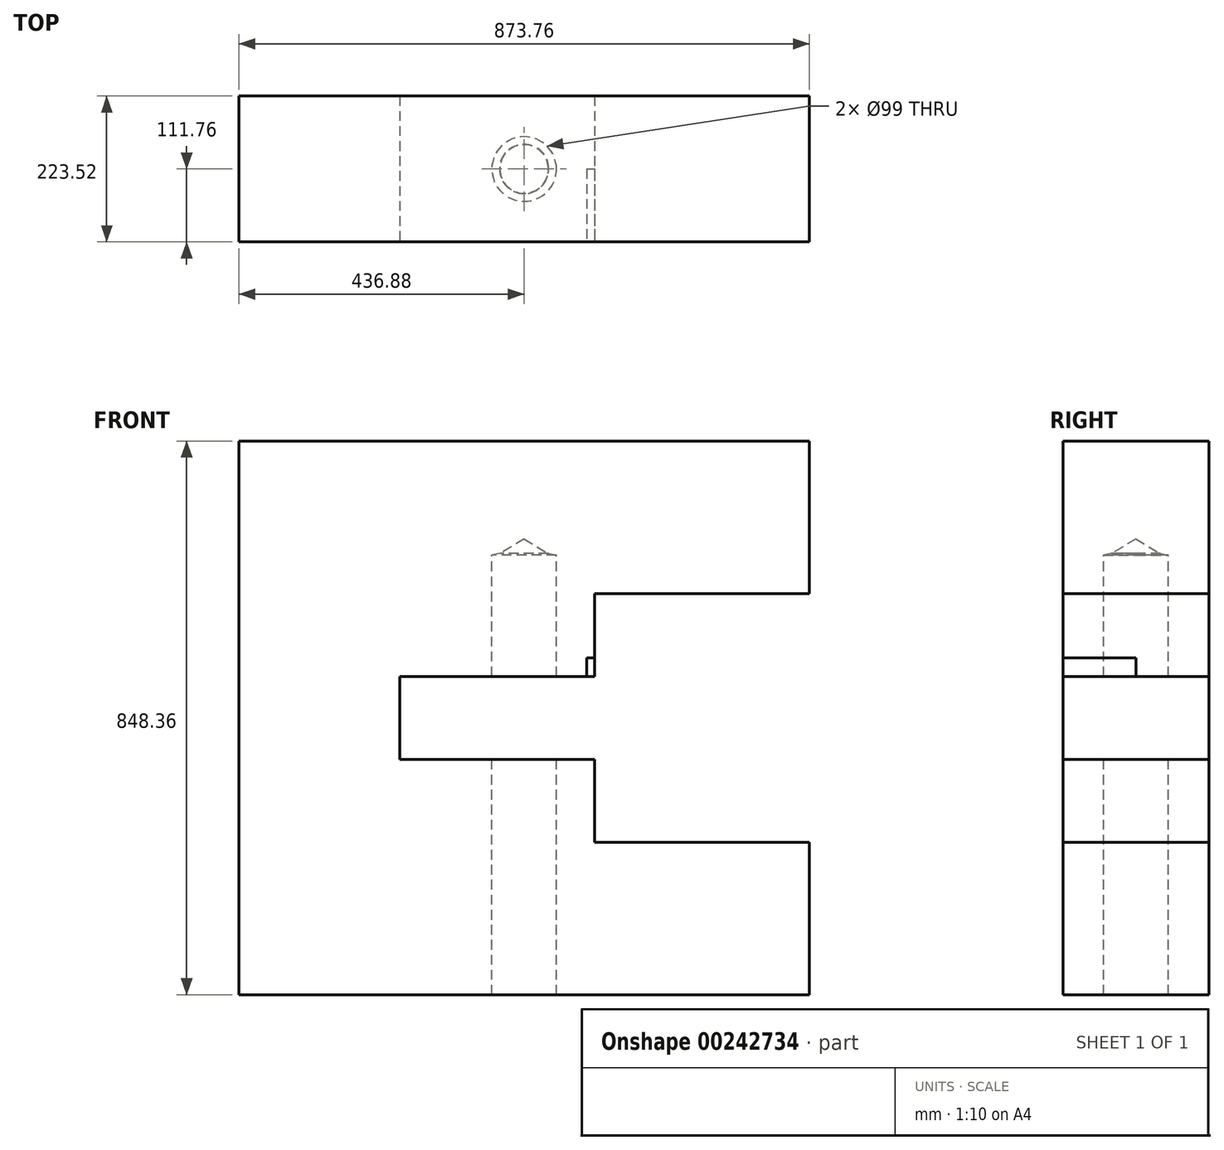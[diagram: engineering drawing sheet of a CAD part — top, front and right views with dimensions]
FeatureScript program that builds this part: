
annotation { "Feature Type Name" : "Feature", "Feature Type Description" : "" }
export const myFeature = defineFeature(function(context is Context, id is Id, definition is map)
    precondition{}
    {
        {
            var Q0;
            Q0=qCreatedBy(makeId("Front.planeOp"),FACE);
            var sketch = newSketch(context, id + "F0", { "sketchPlane" : qUnion([Q0])});
            skLineSegment(sketch, "E0.bottom", {"start": v(-436.88, -424.18) * mm, "end": v(436.88, -424.18) * mm});
            skLineSegment(sketch, "E0.top", {"start": v(-436.88, 424.18) * mm, "end": v(436.88, 424.18) * mm});
            skLineSegment(sketch, "E0.left", {"start": v(-436.88, -424.18) * mm, "end": v(-436.88, 424.18) * mm});
            skLineSegment(sketch, "E0.right", {"start": v(436.88, -424.18) * mm, "end": v(436.88, 424.18) * mm});
            skPoint(sketch, "E0.middle", {"position": v(0, 0) * mm});
            skSolve(sketch);
        }
        {
            var Q0;
            Q0 = qSketchRegion(id + "F0", true);
            extrude(context, id + "F1", {"entities" : qUnion([Q0]), "depth" : 223.52 * mm});
        }
        {
            var Q0;
            Q0=makeQuery(id+"F1.opExtrude","CAP_FACE",FACE,{"disambiguationData":[OSD([sQuery(id+"F0.wireOp",EDGE,"E0.bottom"),sQuery(id+"F0.wireOp",EDGE,"E0.top"),sQuery(id+"F0.wireOp",EDGE,"E0.left"),sQuery(id+"F0.wireOp",EDGE,"E0.right")])],"isStart":false});
            var sketch = newSketch(context, id + "F2", { "sketchPlane" : qUnion([Q0])});
            skLineSegment(sketch, "E1.0", {"start": v(107.7, 63.5) * mm, "end": v(-190.5, 63.5) * mm});
            skLineSegment(sketch, "E2", {"start": v(-190.5, 48.9) * mm, "end": v(-190.5, 0) * mm});
            skLineSegment(sketch, "E3", {"start": v(-190.5, 48.9) * mm, "end": v(-190.5, 63.5) * mm});
            skLineSegment(sketch, "E4", {"start": v(107.7, 181.23) * mm, "end": v(107.7, 85.35) * mm});
            skLineSegment(sketch, "E5", {"start": v(107.7, 190.5) * mm, "end": v(430.53, 190.5) * mm});
            skLineSegment(sketch, "E6", {"start": v(107.7, 85.35) * mm, "end": v(107.7, 63.5) * mm});
            skLineSegment(sketch, "E7", {"start": v(107.7, 181.23) * mm, "end": v(107.7, 190.5) * mm});
            skPoint(sketch, "E8.orphan", {"position": v(0, 63.5) * mm});
            skPoint(sketch, "E9.orphan", {"position": v(107.7, 0) * mm});
            skLineSegment(sketch, "E10.MirrorCS", {"start": v(107.7, -190.5) * mm, "end": v(716.46, -190.5) * mm});
            skLineSegment(sketch, "E11.MirrorCS", {"start": v(107.7, -181.23) * mm, "end": v(107.7, -85.35) * mm});
            skLineSegment(sketch, "E12.MirrorCS", {"start": v(107.7, -63.5) * mm, "end": v(-190.5, -63.5) * mm});
            skLineSegment(sketch, "E13.MirrorCS", {"start": v(107.7, -85.35) * mm, "end": v(107.7, -63.5) * mm});
            skLineSegment(sketch, "E14.MirrorCS", {"start": v(-190.5, -48.9) * mm, "end": v(-190.5, -63.5) * mm});
            skLineSegment(sketch, "E15.MirrorCS", {"start": v(-190.5, -48.9) * mm, "end": v(-190.5, 0) * mm});
            skLineSegment(sketch, "E16", {"start": v(430.53, 190.5) * mm, "end": v(716.46, 190.5) * mm});
            skLineSegment(sketch, "E17", {"start": v(716.46, 190.5) * mm, "end": v(716.46, -190.5) * mm});
            skLineSegment(sketch, "E18", {"start": v(107.7, -181.23) * mm, "end": v(107.7, -190.5) * mm});
            skSolve(sketch);
        }
        {
            var Q0;
            Q0 = qSketchRegion(id + "F2", true);
            extrude(context, id + "F3", {"entities" : qUnion([Q0]), "operationType" : NewBodyOperationType.REMOVE, "oppositeDirection" : true, "depth" : 254 * mm});
        }
        {
            var Q0;
            Q0=makeQuery(id+"F1.opExtrude","SWEPT_FACE",FACE,{"disambiguationData":[OSD([sQuery(id+"F0.wireOp",EDGE,"E0.bottom")])]});
            var sketch = newSketch(context, id + "F4", { "sketchPlane" : qUnion([Q0])});
            skPoint(sketch, "E19", {"position": v(0, 111.76) * mm});
            skLineSegment(sketch, "E20", {"start": v(-436.88, 111.76) * mm, "end": v(436.88, 111.76) * mm});
            skCircle(sketch, "E21", {"center": v(0, 111.76) * mm, "radius": 49.53 * mm});
            skSolve(sketch);
        }
        {
            var Q0;
            Q0=sQuery(id+"F4.wireOp",VERTEX,"E19");
            var Q1;
            Q1=makeQuery(id+"F1.opExtrude","SWEPT_BODY",BODY,{"disambiguationData":[OSD([sQuery(id+"F0.wireOp",EDGE,"E0.bottom"),sQuery(id+"F0.wireOp",EDGE,"E0.top"),sQuery(id+"F0.wireOp",EDGE,"E0.left"),sQuery(id+"F0.wireOp",EDGE,"E0.right")])]});
            hole(context, id + "F5", {"style" : HoleStyle.SIMPLE, "endStyle" : HoleEndStyle.BLIND, "holeDiameter" : 75 * mm, "holeDepth" : 675.64 * mm, "locations" : qUnion([Q0]), "scope" : qUnion([Q1]), "tappedDepth" : 12 * mm, "tapClearance" : 3});
        }
        {
            var Q0;
            Q0=qCreatedBy(makeId("Front.planeOp"),FACE);
            cPlane(context, id + "F6", {"entities" : qUnion([Q0]), "cplaneType" : CPlaneType.OFFSET, "offset" : 111.76 * mm, "width" : 152.4 * mm, "height" : 152.4 * mm});
        }
        {
            var Q0;
            Q0=makeQuery(id+"F1.opExtrude","CAP_FACE",FACE,{"disambiguationData":[OSD([sQuery(id+"F0.wireOp",EDGE,"E0.bottom"),sQuery(id+"F0.wireOp",EDGE,"E0.top"),sQuery(id+"F0.wireOp",EDGE,"E0.left"),sQuery(id+"F0.wireOp",EDGE,"E0.right")])],"isStart":false});
            var sketch = newSketch(context, id + "F7", { "sketchPlane" : qUnion([Q0])});
            skLineSegment(sketch, "E22.bottom", {"start": v(118.46, 91.75) * mm, "end": v(95.92, 91.75) * mm});
            skLineSegment(sketch, "E22.top", {"start": v(118.46, 46.67) * mm, "end": v(95.92, 46.67) * mm});
            skLineSegment(sketch, "E22.left", {"start": v(118.46, 91.75) * mm, "end": v(118.46, 46.67) * mm});
            skLineSegment(sketch, "E22.right", {"start": v(95.92, 91.75) * mm, "end": v(95.92, 46.67) * mm});
            skSolve(sketch);
        }
        {
            var Q0;
            Q0 = qSketchRegion(id + "F7", true);
            extrude(context, id + "F8", {"entities" : qUnion([Q0]), "operationType" : NewBodyOperationType.REMOVE, "oppositeDirection" : true, "depth" : 111.76 * mm});
        }
        {
            var Q0;
            Q0=qCreatedBy(id+"F6.planeOp",FACE);
            var sketch = newSketch(context, id + "F9", { "sketchPlane" : qUnion([Q0])});
            skLineSegment(sketch, "E23", {"start": v(0, -4.85) * mm, "end": v(0, 519.29) * mm});
            skLineSegment(sketch, "E24.0", {"start": v(49.5, -428.16) * mm, "end": v(49.5, 249.03) * mm});
            skLineSegment(sketch, "E25", {"start": v(18.88, 251.64) * mm, "end": v(37.75, 251.64) * mm});
            skLineSegment(sketch, "E26", {"start": v(37.75, 251.64) * mm, "end": v(49.5, 249.03) * mm});
            skLineSegment(sketch, "E27", {"start": v(49.5, -428.16) * mm, "end": v(8.59, -428.16) * mm});
            skLineSegment(sketch, "E28", {"start": v(8.59, -428.16) * mm, "end": v(18.88, 251.64) * mm});
            skPoint(sketch, "E29.orphan", {"position": v(0, 251.64) * mm});
            skSolve(sketch);
        }
        {
            var Q0;
            Q0 = qSketchRegion(id + "F9", true);
            var Q1;
            Q1=sQuery(id+"F9.wireOp",EDGE,"E23");
            revolve(context, id + "F10", {"operationType" : NewBodyOperationType.REMOVE, "entities" : qUnion([Q0]), "axis" : qUnion([Q1]), "revolveType" : RevolveType.FULL, "oppositeDirection" : true});
        }
    });
